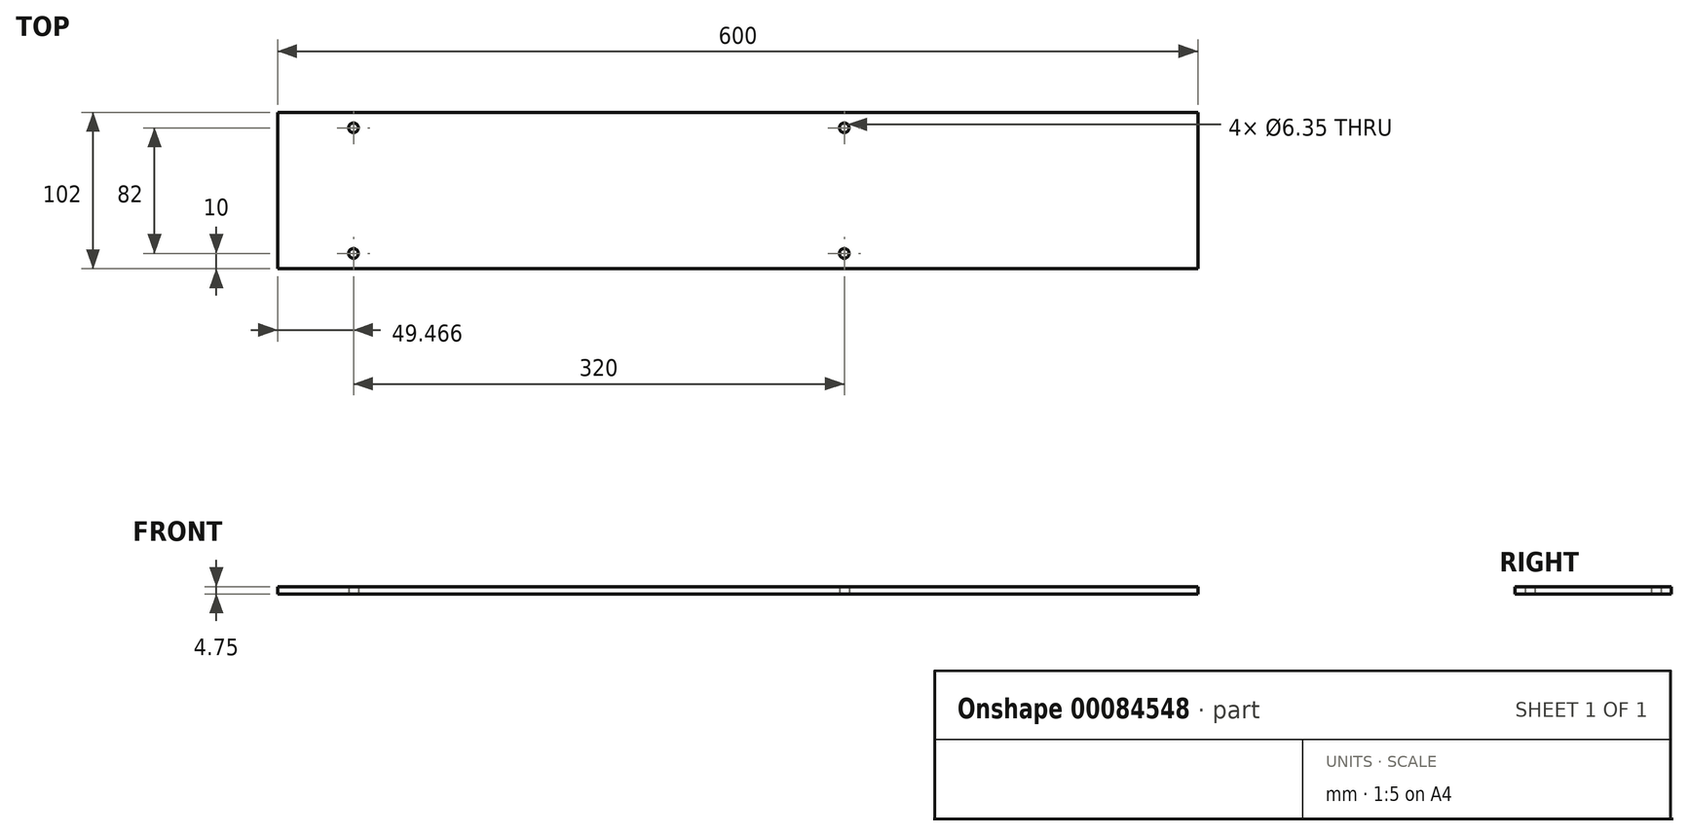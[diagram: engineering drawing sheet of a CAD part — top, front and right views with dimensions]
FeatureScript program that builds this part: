
annotation { "Feature Type Name" : "Feature", "Feature Type Description" : "" }
export const myFeature = defineFeature(function(context is Context, id is Id, definition is map)
    precondition{}
    {
        {
            assignVariable(context, id + "F0", {"name" : "al_2", "value" : 4.75});
        }
        {
            var Q0;
            Q0=qCreatedBy(makeId("Top.planeOp"),FACE);
            var sketch = newSketch(context, id + "F1", { "sketchPlane" : qUnion([Q0]) });
            skLineSegment(sketch, "E0.bottom", {"start": v(300, -51) * mm, "end": v(-300, -51) * mm});
            skLineSegment(sketch, "E0.top", {"start": v(300, 51) * mm, "end": v(-300, 51) * mm});
            skLineSegment(sketch, "E0.left", {"start": v(300, -51) * mm, "end": v(300, 51) * mm});
            skLineSegment(sketch, "E0.right", {"start": v(-300, -51) * mm, "end": v(-300, 51) * mm});
            skPoint(sketch, "E0.middle", {"position": v(0, 0) * mm});
            skLineSegment(sketch, "E1.bottom", {"start": v(69.47, -41) * mm, "end": v(-250.53, -41) * mm, "construction": true});
            skLineSegment(sketch, "E1.top", {"start": v(69.47, 41) * mm, "end": v(-250.53, 41) * mm, "construction": true});
            skLineSegment(sketch, "E1.left", {"start": v(69.47, -41) * mm, "end": v(69.47, 41) * mm, "construction": true});
            skLineSegment(sketch, "E1.right", {"start": v(-250.53, -41) * mm, "end": v(-250.53, 41) * mm, "construction": true});
            skPoint(sketch, "E1.middle", {"position": v(-90.53, 0) * mm});
            skCircle(sketch, "E2", {"center": v(-250.53, 41) * mm, "radius": 3.18 * mm});
            skCircle(sketch, "E3", {"center": v(69.47, 41) * mm, "radius": 3.18 * mm});
            skCircle(sketch, "E4", {"center": v(-250.53, -41) * mm, "radius": 3.18 * mm});
            skCircle(sketch, "E5", {"center": v(69.47, -41) * mm, "radius": 3.18 * mm});
            skSolve(sketch);
        }
        {
            var Q0;
            Q0 = qSketchRegion(id + "F1", true);
            extrude(context, id + "F2", {"entities" : qUnion([Q0]), "depth" : (getVariable(context, 'al_2')) * mm});
        }
    });
